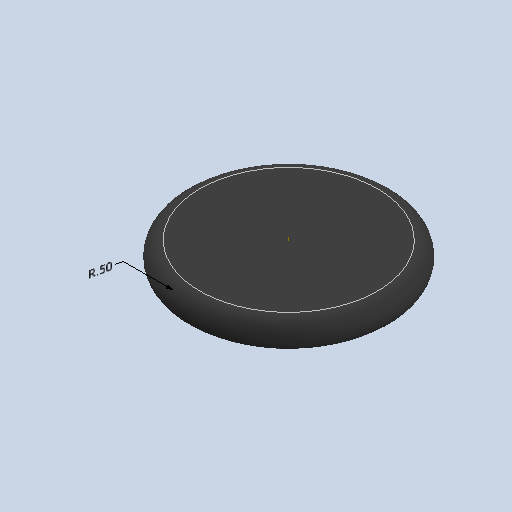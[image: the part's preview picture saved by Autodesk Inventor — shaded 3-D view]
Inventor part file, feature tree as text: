
AUTODESK INVENTOR PART (.ipt)
format: ipt  version: 2022 (Build 260153000, 153)  size: 122,368 bytes
history: native  units: in
note: dims shown in document units (in); Inventor stores cm internally (conversion verified against a paired STEP export)
features: other x2, extrude x1, fillet x1, sketch x1
ambient origin geometry x8: Origin, YZ Plane, XZ Plane, XY Plane, X Axis, Y Axis, Z Axis, Center Point
bodies: Solid1 (feature_tree)
feature tree (5):
  other  "Annotations"
  extrude  "Extrusion1"  Depth=1.0in TaperAngle=0.0deg
  fillet  "Fillet1"  Radius=0.5in
  sketch  "Sketch1"  dims[d0=7.25in d1=1.0in d2=0.0in d3=0.5in d4=0.2564in d5=0.1843in d6=0.5in]
  other  "Radial Dimension 1"
